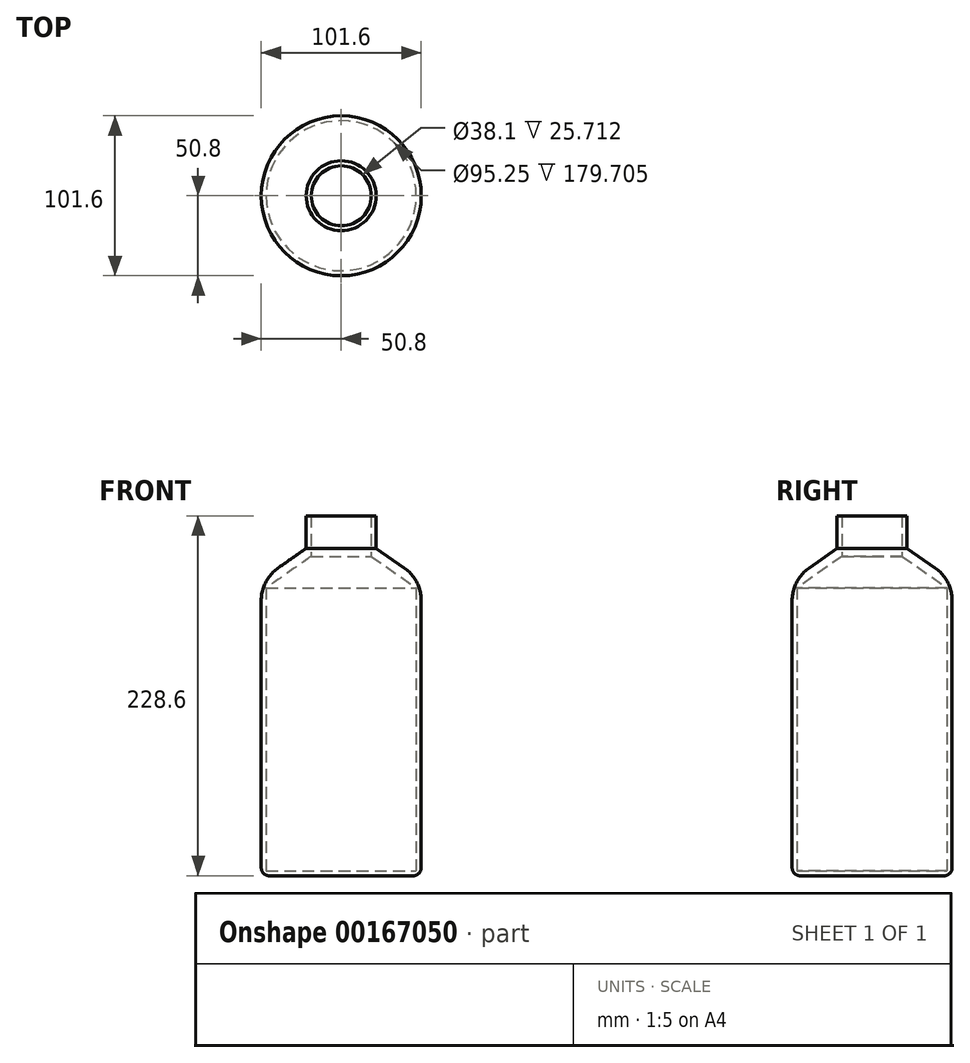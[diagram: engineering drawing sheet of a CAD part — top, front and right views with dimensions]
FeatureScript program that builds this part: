
annotation { "Feature Type Name" : "Feature", "Feature Type Description" : "" }
export const myFeature = defineFeature(function(context is Context, id is Id, definition is map)
    precondition{}
    {
        {
            var Q0;
            Q0=qCreatedBy(makeId("Front.planeOp"),FACE);
            var sketch = newSketch(context, id + "F0", { "sketchPlane" : qUnion([Q0])});
            skLineSegment(sketch, "E0", {"start": v(0, 0) * mm, "end": v(0, 228.6) * mm, "construction": true});
            skLineSegment(sketch, "E1.bottom", {"start": v(19.05, 228.6) * mm, "end": v(22.22, 228.6) * mm});
            skLineSegment(sketch, "E1.left", {"start": v(19.05, 228.6) * mm, "end": v(19.05, 202.89) * mm});
            skLineSegment(sketch, "E1.right", {"start": v(22.22, 228.6) * mm, "end": v(22.22, 207.97) * mm});
            skLineSegment(sketch, "E2.top", {"start": v(47.63, 0) * mm, "end": v(50.8, 0) * mm});
            skLineSegment(sketch, "E2.left", {"start": v(47.63, 182.88) * mm, "end": v(47.63, 3.17) * mm});
            skLineSegment(sketch, "E2.right", {"start": v(50.8, 187.96) * mm, "end": v(50.8, 0) * mm});
            skLineSegment(sketch, "E3.bottom", {"start": v(47.63, 0) * mm, "end": v(0, 0) * mm});
            skLineSegment(sketch, "E3.top", {"start": v(47.63, 3.17) * mm, "end": v(0, 3.17) * mm});
            skLineSegment(sketch, "E3.right", {"start": v(0, 0) * mm, "end": v(0, 3.17) * mm});
            skLineSegment(sketch, "E4", {"start": v(22.22, 207.97) * mm, "end": v(50.8, 187.96) * mm});
            skLineSegment(sketch, "E5", {"start": v(19.05, 202.89) * mm, "end": v(47.63, 182.88) * mm});
            skSolve(sketch);
        }
        {
            var Q0;
            Q0 = qSketchRegion(id + "F0", true);
            var Q1;
            Q1=sQuery(id+"F0.wireOp",EDGE,"E0");
            revolve(context, id + "F1", {"entities" : qUnion([Q0]), "axis" : qUnion([Q1]), "revolveType" : RevolveType.FULL});
        }
        {
            var Q0;
            Q0=makeQuery(id+"F1.opRevolve","SWEPT_EDGE",EDGE,{"disambiguationData":[OSD([sQuery(id+"F0.wireOp",EDGE,"E2.right"),sQuery(id+"F0.wireOp",EDGE,"E4")])]});
            fillet(context, id + "F2", {"entities" : qUnion([Q0]), "radius" : 25.4 * mm, "tangentPropagation" : true, "allowEdgeOverflow" : false});
        }
        {
            var Q0;
            Q0=makeQuery(id+"F1.opRevolve","SWEPT_EDGE",EDGE,{"disambiguationData":[OSD([sQuery(id+"F0.wireOp",EDGE,"E2.top"),sQuery(id+"F0.wireOp",EDGE,"E2.right")])]});
            fillet(context, id + "F3", {"entities" : qUnion([Q0]), "radius" : 5.08 * mm, "tangentPropagation" : true, "allowEdgeOverflow" : false});
        }
    });
